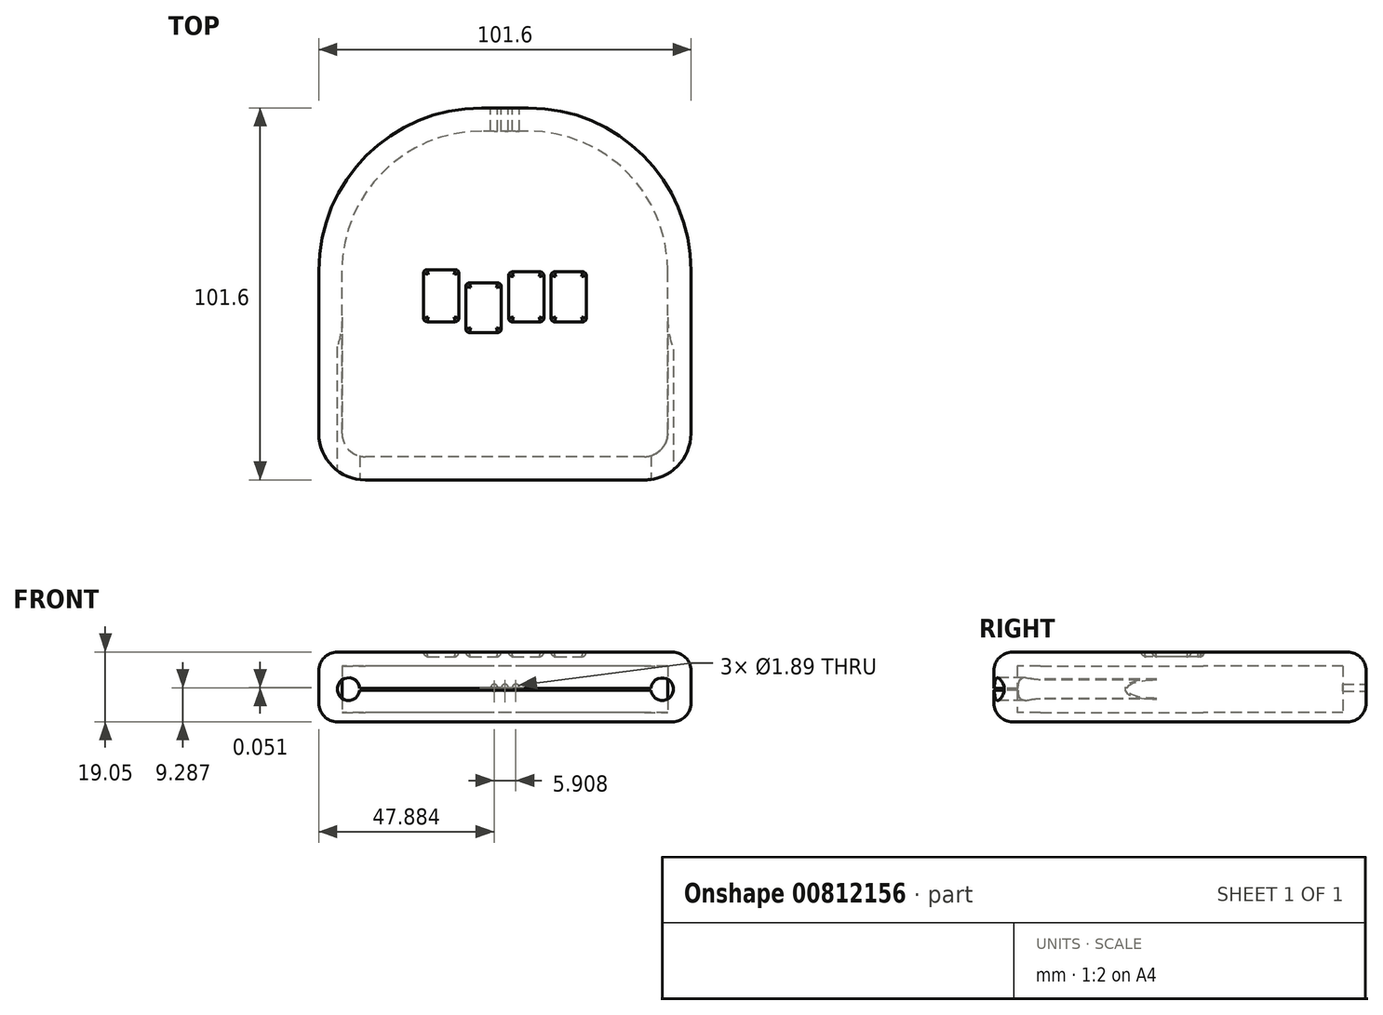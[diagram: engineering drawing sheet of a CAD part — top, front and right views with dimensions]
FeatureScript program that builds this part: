
annotation { "Feature Type Name" : "Feature", "Feature Type Description" : "" }
export const myFeature = defineFeature(function(context is Context, id is Id, definition is map)
    precondition{}
    {
        {
            var Q0;
            Q0=qCreatedBy(makeId("Top.planeOp"),FACE);
            cPlane(context, id + "F0", {"entities" : qUnion([Q0]), "cplaneType" : CPlaneType.OFFSET, "offset" : 2.54 * mm, "width" : 152.4 * mm, "height" : 152.4 * mm});
        }
        {
            var Q0;
            Q0=qCreatedBy(id+"F0.planeOp",FACE);
            var sketch = newSketch(context, id + "F1", { "sketchPlane" : qUnion([Q0])});
            skLineSegment(sketch, "E0.bottom", {"start": v(38.1, -44.45) * mm, "end": v(-38.1, -44.45) * mm});
            skLineSegment(sketch, "E0.top", {"start": v(6.35, 44.45) * mm, "end": v(-6.35, 44.45) * mm});
            skLineSegment(sketch, "E0.left", {"start": v(44.45, -38.1) * mm, "end": v(44.45, 6.35) * mm});
            skLineSegment(sketch, "E0.right", {"start": v(-44.45, -38.1) * mm, "end": v(-44.45, 6.35) * mm});
            skPoint(sketch, "E0.middle", {"position": v(0, 0) * mm});
            skPoint(sketch, "E1.visualSharp", {"position": v(-44.45, 44.45) * mm});
            skArc(sketch, "E1.filletArc", {"start": v(-6.35, 44.45) * mm, "mid": v(-33.3, 33.3) * mm, "end": v(-44.45, 6.35) * mm});
            skPoint(sketch, "E2.visualSharp", {"position": v(44.45, 44.45) * mm});
            skArc(sketch, "E2.filletArc", {"start": v(44.45, 6.35) * mm, "mid": v(33.3, 33.3) * mm, "end": v(6.35, 44.45) * mm});
            skPoint(sketch, "E3.visualSharp", {"position": v(-44.45, -44.45) * mm});
            skArc(sketch, "E3.filletArc", {"start": v(-44.45, -38.1) * mm, "mid": v(-42.6, -42.6) * mm, "end": v(-38.1, -44.45) * mm});
            skPoint(sketch, "E4.visualSharp", {"position": v(44.45, -44.45) * mm});
            skArc(sketch, "E4.filletArc", {"start": v(38.1, -44.45) * mm, "mid": v(42.6, -42.6) * mm, "end": v(44.45, -38.1) * mm});
            skSolve(sketch);
        }
        {
            var Q0;
            Q0=qCreatedBy(makeId("Top.planeOp"),FACE);
            var sketch = newSketch(context, id + "F2", { "sketchPlane" : qUnion([Q0])});
            skLineSegment(sketch, "E5.0", {"start": v(6.35, 50.8) * mm, "end": v(-6.35, 50.8) * mm});
            skArc(sketch, "E5.1", {"start": v(50.8, 6.35) * mm, "mid": v(37.78, 37.78) * mm, "end": v(6.35, 50.8) * mm});
            skArc(sketch, "E5.2", {"start": v(-6.35, 50.8) * mm, "mid": v(-37.78, 37.78) * mm, "end": v(-50.8, 6.35) * mm});
            skLineSegment(sketch, "E5.3", {"start": v(50.8, -38.1) * mm, "end": v(50.8, 6.35) * mm});
            skLineSegment(sketch, "E5.4", {"start": v(-50.8, -38.1) * mm, "end": v(-50.8, 6.35) * mm});
            skArc(sketch, "E5.5", {"start": v(-50.8, -38.1) * mm, "mid": v(-47.08, -47.08) * mm, "end": v(-38.1, -50.8) * mm});
            skLineSegment(sketch, "E5.6", {"start": v(38.1, -50.8) * mm, "end": v(-38.1, -50.8) * mm});
            skArc(sketch, "E5.7", {"start": v(38.1, -50.8) * mm, "mid": v(47.08, -47.08) * mm, "end": v(50.8, -38.1) * mm});
            skSolve(sketch);
        }
        {
            var Q0;
            Q0=qSketchRegion(id+"F2",true);
            extrude(context, id + "F3", {"entities" : qUnion([Q0]), "depth" : 19.05 * mm, "offsetDistance" : 25.4 * mm});
        }
        {
            var Q0;
            Q0=makeQuery(id+"F3.opExtrude","CAP_FACE",FACE,{"disambiguationData":[OSD([sQuery(id+"F2.wireOp",EDGE,"E5.0"),sQuery(id+"F2.wireOp",EDGE,"E5.1"),sQuery(id+"F2.wireOp",EDGE,"E5.2"),sQuery(id+"F2.wireOp",EDGE,"E5.3"),sQuery(id+"F2.wireOp",EDGE,"E5.4"),sQuery(id+"F2.wireOp",EDGE,"E5.5"),sQuery(id+"F2.wireOp",EDGE,"E5.6"),sQuery(id+"F2.wireOp",EDGE,"E5.7")])],"isStart":false});
            var Q1;
            Q1 = qSketchRegion(id + "F1", true);
            extrude(context, id + "F4", {"entities" : qUnion([Q0, Q1]), "operationType" : NewBodyOperationType.REMOVE, "depth" : 12.7 * mm, "offsetDistance" : 25.4 * mm});
        }
        {
            var Q0;
            Q0=makeQuery(id+"F3.opExtrude","CAP_EDGE",EDGE,{"disambiguationData":[OSD([sQuery(id+"F2.wireOp",EDGE,"E5.5")])],"isStart":false});
            fillet(context, id + "F5", {"entities" : qUnion([Q0]), "radius" : 5.08 * mm, "tangentPropagation" : true, "allowEdgeOverflow" : false});
        }
        {
            var Q0;
            Q0=makeQuery(id+"F3.opExtrude","CAP_EDGE",EDGE,{"disambiguationData":[OSD([sQuery(id+"F2.wireOp",EDGE,"E5.3")])],"isStart":true});
            fillet(context, id + "F6", {"entities" : qUnion([Q0]), "radius" : 5.08 * mm, "tangentPropagation" : true, "allowEdgeOverflow" : false});
        }
        {
            var Q0;
            Q0=qCreatedBy(makeId("Top.planeOp"),FACE);
            cPlane(context, id + "F7", {"entities" : qUnion([Q0]), "cplaneType" : CPlaneType.OFFSET, "offset" : 19.05 * mm, "width" : 152.4 * mm, "height" : 152.4 * mm});
        }
        {
            var Q0;
            Q0=qCreatedBy(id+"F7.planeOp",FACE);
            var sketch = newSketch(context, id + "F8", { "sketchPlane" : qUnion([Q0])});
            skLineSegment(sketch, "E6.bottom", {"start": v(-21.17, 6.64) * mm, "end": v(-13.57, 6.64) * mm});
            skLineSegment(sketch, "E6.top", {"start": v(-21.17, -7.6) * mm, "end": v(-13.57, -7.6) * mm});
            skLineSegment(sketch, "E6.left", {"start": v(-22.19, 5.62) * mm, "end": v(-22.19, -6.58) * mm});
            skLineSegment(sketch, "E6.right", {"start": v(-12.56, 5.62) * mm, "end": v(-12.56, -6.58) * mm});
            skPoint(sketch, "E7.visualSharp", {"position": v(-12.56, 6.64) * mm});
            skArc(sketch, "E7.filletArc", {"start": v(-12.56, 5.62) * mm, "mid": v(-12.85, 6.34) * mm, "end": v(-13.57, 6.64) * mm});
            skPoint(sketch, "E8.visualSharp", {"position": v(-22.19, 6.64) * mm});
            skArc(sketch, "E8.filletArc", {"start": v(-21.17, 6.64) * mm, "mid": v(-21.9, 6.34) * mm, "end": v(-22.19, 5.62) * mm});
            skPoint(sketch, "E9.visualSharp", {"position": v(-22.19, -7.6) * mm});
            skArc(sketch, "E9.filletArc", {"start": v(-22.19, -6.58) * mm, "mid": v(-21.9, -7.3) * mm, "end": v(-21.17, -7.6) * mm});
            skPoint(sketch, "E10.visualSharp", {"position": v(-12.56, -7.6) * mm});
            skArc(sketch, "E10.filletArc", {"start": v(-13.57, -7.6) * mm, "mid": v(-12.85, -7.3) * mm, "end": v(-12.56, -6.58) * mm});
            skLineSegment(sketch, "E11.bottom", {"start": v(-9.62, 3.05) * mm, "end": v(-2.02, 3.05) * mm});
            skLineSegment(sketch, "E11.top", {"start": v(-9.62, -10.58) * mm, "end": v(-2.02, -10.58) * mm});
            skLineSegment(sketch, "E11.left", {"start": v(-10.63, 2.04) * mm, "end": v(-10.63, -9.57) * mm});
            skLineSegment(sketch, "E11.right", {"start": v(-1, 2.04) * mm, "end": v(-1, -9.57) * mm});
            skArc(sketch, "E12.filletArc", {"start": v(-1, 2.04) * mm, "mid": v(-1.3, 2.75) * mm, "end": v(-2.02, 3.05) * mm});
            skArc(sketch, "E13.filletArc", {"start": v(-9.62, 3.05) * mm, "mid": v(-10.34, 2.75) * mm, "end": v(-10.63, 2.04) * mm});
            skArc(sketch, "E14.filletArc", {"start": v(-10.63, -9.57) * mm, "mid": v(-10.34, -10.28) * mm, "end": v(-9.62, -10.58) * mm});
            skArc(sketch, "E15.filletArc", {"start": v(-2.02, -10.58) * mm, "mid": v(-1.3, -10.28) * mm, "end": v(-1, -9.57) * mm});
            skLineSegment(sketch, "E16.bottom", {"start": v(2.03, 6) * mm, "end": v(9.63, 6) * mm});
            skLineSegment(sketch, "E16.top", {"start": v(2.03, -7.63) * mm, "end": v(9.63, -7.63) * mm});
            skLineSegment(sketch, "E16.left", {"start": v(1.02, 4.99) * mm, "end": v(1.02, -6.61) * mm});
            skLineSegment(sketch, "E16.right", {"start": v(10.65, 4.99) * mm, "end": v(10.65, -6.61) * mm});
            skArc(sketch, "E17.filletArc", {"start": v(10.65, 4.99) * mm, "mid": v(10.35, 5.7) * mm, "end": v(9.63, 6) * mm});
            skArc(sketch, "E18.filletArc", {"start": v(2.03, 6) * mm, "mid": v(1.31, 5.7) * mm, "end": v(1.02, 4.99) * mm});
            skArc(sketch, "E19.filletArc", {"start": v(1.02, -6.61) * mm, "mid": v(1.31, -7.33) * mm, "end": v(2.03, -7.63) * mm});
            skArc(sketch, "E20.filletArc", {"start": v(9.63, -7.63) * mm, "mid": v(10.35, -7.33) * mm, "end": v(10.65, -6.61) * mm});
            skLineSegment(sketch, "E21.bottom", {"start": v(13.61, 6.02) * mm, "end": v(21.21, 6.02) * mm});
            skLineSegment(sketch, "E21.top", {"start": v(13.61, -7.62) * mm, "end": v(21.21, -7.62) * mm});
            skLineSegment(sketch, "E21.left", {"start": v(12.6, 5) * mm, "end": v(12.6, -6.6) * mm});
            skLineSegment(sketch, "E21.right", {"start": v(22.23, 5) * mm, "end": v(22.23, -6.6) * mm});
            skArc(sketch, "E22.filletArc", {"start": v(22.23, 5) * mm, "mid": v(21.93, 5.72) * mm, "end": v(21.21, 6.02) * mm});
            skArc(sketch, "E23.filletArc", {"start": v(13.61, 6.02) * mm, "mid": v(12.9, 5.72) * mm, "end": v(12.6, 5) * mm});
            skArc(sketch, "E24.filletArc", {"start": v(12.6, -6.6) * mm, "mid": v(12.9, -7.32) * mm, "end": v(13.61, -7.62) * mm});
            skArc(sketch, "E25.filletArc", {"start": v(21.21, -7.62) * mm, "mid": v(21.93, -7.32) * mm, "end": v(22.23, -6.6) * mm});
            skSolve(sketch);
        }
        {
            var Q0;
            Q0=makeQuery(id+"F8.imprint","IMPRINT",FACE,{"disambiguationData":[TD([[makeQuery(id+"F8.imprint","IMPRINT",EDGE,{"derivedFrom":sQuery(id+"F8.wireOp",EDGE,"E6.bottom")}),-1.0]])]});
            var Q1;
            Q1=makeQuery(id+"F8.imprint","IMPRINT",FACE,{"disambiguationData":[TD([[makeQuery(id+"F8.imprint","IMPRINT",EDGE,{"derivedFrom":sQuery(id+"F8.wireOp",EDGE,"E11.bottom")}),-1.0]])]});
            var Q2;
            Q2=makeQuery(id+"F8.imprint","IMPRINT",FACE,{"disambiguationData":[TD([[makeQuery(id+"F8.imprint","IMPRINT",EDGE,{"derivedFrom":sQuery(id+"F8.wireOp",EDGE,"E16.bottom")}),-1.0]])]});
            var Q3;
            Q3=makeQuery(id+"F8.imprint","IMPRINT",FACE,{"disambiguationData":[TD([[makeQuery(id+"F8.imprint","IMPRINT",EDGE,{"derivedFrom":sQuery(id+"F8.wireOp",EDGE,"E21.bottom")}),-1.0]])]});
            extrude(context, id + "F9", {"entities" : qUnion([Q0, Q1, Q2, Q3]), "operationType" : NewBodyOperationType.REMOVE, "oppositeDirection" : true, "depth" : 1.27 * mm, "offsetDistance" : 25.4 * mm});
        }
        {
            var Q0;
            Q0=makeQuery(id+"F9.boolean.opBoolean","COPY",EDGE,{"derivedFrom":makeQuery(id+"F9.opExtrude","CAP_EDGE",EDGE,{"disambiguationData":[OSD([sQuery(id+"F8.wireOp",EDGE,"E6.bottom")])],"isStart":false})});
            var Q1;
            Q1=makeQuery(id+"F9.boolean.opBoolean","COPY",EDGE,{"derivedFrom":makeQuery(id+"F9.opExtrude","CAP_EDGE",EDGE,{"disambiguationData":[OSD([sQuery(id+"F8.wireOp",EDGE,"E11.bottom")])],"isStart":false})});
            var Q2;
            Q2=makeQuery(id+"F9.boolean.opBoolean","COPY",EDGE,{"derivedFrom":makeQuery(id+"F9.opExtrude","CAP_EDGE",EDGE,{"disambiguationData":[OSD([sQuery(id+"F8.wireOp",EDGE,"E16.bottom")])],"isStart":false})});
            var Q3;
            Q3=makeQuery(id+"F9.boolean.opBoolean","COPY",EDGE,{"derivedFrom":makeQuery(id+"F9.opExtrude","CAP_EDGE",EDGE,{"disambiguationData":[OSD([sQuery(id+"F8.wireOp",EDGE,"E21.bottom")])],"isStart":false})});
            fillet(context, id + "F10", {"entities" : qUnion([Q0, Q1, Q2, Q3]), "radius" : 1.27 * mm, "tangentPropagation" : true, "allowEdgeOverflow" : false});
        }
        {
            var Q0;
            Q0=makeQuery(id+"F3.opExtrude","SWEPT_FACE",FACE,{"disambiguationData":[OSD([sQuery(id+"F2.wireOp",EDGE,"E5.6")])]});
            var sketch = newSketch(context, id + "F11", { "sketchPlane" : qUnion([Q0])});
            skLineSegment(sketch, "E26.bottom", {"start": v(44.26, 9.18) * mm, "end": v(-44.26, 9.18) * mm});
            skLineSegment(sketch, "E26.top", {"start": v(44.26, 8.66) * mm, "end": v(-44.26, 8.66) * mm});
            skLineSegment(sketch, "E26.left", {"start": v(44.26, 9.18) * mm, "end": v(44.26, 8.66) * mm});
            skLineSegment(sketch, "E26.right", {"start": v(-44.26, 9.18) * mm, "end": v(-44.26, 8.66) * mm});
            skPoint(sketch, "E26.middle", {"position": v(0, 8.92) * mm});
            skCircle(sketch, "E27", {"center": v(42.94, 8.92) * mm, "radius": 3.08 * mm});
            skCircle(sketch, "E28", {"center": v(-42.68, 8.92) * mm, "radius": 3.09 * mm});
            skSolve(sketch);
        }
        {
            var Q0;
            {var subQ0=sQuery(id+"F11.wireOp",EDGE,"E26.left");Q0=makeQuery(id+"F11.imprint","IMPRINT",FACE,{"disambiguationData":[TD([[makeQuery(id+"F11.imprint","IMPRINT",EDGE,{"derivedFrom":subQ0}),1.0]])]});}
            var Q1;
            {var subQ0=sQuery(id+"F11.wireOp",EDGE,"E26.bottom");var subQ1=sQuery(id+"F2.wireOp",EDGE,"E5.6");var subQ2=makeQuery(id+"F3.opExtrude","SWEPT_EDGE",EDGE,{"disambiguationData":[OSD([subQ1,sQuery(id+"F2.wireOp",EDGE,"E5.7")])]});var subQ3=makeQuery(id+"F11.imprint","INTERSECT",VERTEX,{"derivedFrom":[subQ2,subQ0]});Q1=makeQuery(id+"F11.imprint","IMPRINT",FACE,{"disambiguationData":[TD([[makeQuery(id+"F11.imprint","IMPRINT",EDGE,{"disambiguationData":[TD([[subQ3,-1.0]])],"derivedFrom":subQ0}),1.0]])]});}
            var Q2;
            {var subQ0=sQuery(id+"F11.wireOp",EDGE,"E27");var subQ1=sQuery(id+"F11.wireOp",EDGE,"E26.bottom");var subQ2=makeQuery(id+"F11.imprint","INTERSECT",VERTEX,{"derivedFrom":[subQ1,subQ0]});Q2=makeQuery(id+"F11.imprint","IMPRINT",FACE,{"disambiguationData":[TD([[makeQuery(id+"F11.imprint","IMPRINT",EDGE,{"disambiguationData":[TD([[subQ2,-1.0]])],"derivedFrom":subQ0}),-1.0]])]});}
            var Q3;
            {var subQ0=sQuery(id+"F11.wireOp",EDGE,"E26.left");Q3=makeQuery(id+"F11.imprint","IMPRINT",FACE,{"disambiguationData":[TD([[makeQuery(id+"F11.imprint","IMPRINT",EDGE,{"derivedFrom":subQ0}),-1.0]])]});}
            var Q4;
            {var subQ0=sQuery(id+"F11.wireOp",EDGE,"E28");var subQ1=sQuery(id+"F11.wireOp",EDGE,"E26.bottom");var subQ2=makeQuery(id+"F11.imprint","INTERSECT",VERTEX,{"derivedFrom":[subQ1,subQ0]});Q4=makeQuery(id+"F11.imprint","IMPRINT",FACE,{"disambiguationData":[TD([[makeQuery(id+"F11.imprint","IMPRINT",EDGE,{"disambiguationData":[TD([[subQ2,1.0]])],"derivedFrom":subQ0}),-1.0]])]});}
            var Q5;
            {var subQ0=sQuery(id+"F11.wireOp",EDGE,"E26.right");Q5=makeQuery(id+"F11.imprint","IMPRINT",FACE,{"disambiguationData":[TD([[makeQuery(id+"F11.imprint","IMPRINT",EDGE,{"derivedFrom":subQ0}),1.0]])]});}
            var Q6;
            {var subQ0=sQuery(id+"F11.wireOp",EDGE,"E26.right");Q6=makeQuery(id+"F11.imprint","IMPRINT",FACE,{"disambiguationData":[TD([[makeQuery(id+"F11.imprint","IMPRINT",EDGE,{"derivedFrom":subQ0}),-1.0]])]});}
            var Q7;
            Q7=sQuery(id+"F11.wireOp",EDGE,"E27");
            var Q8;
            Q8=sQuery(id+"F11.wireOp",EDGE,"E26.top");
            var Q9;
            Q9=sQuery(id+"F11.wireOp",EDGE,"E26.bottom");
            var Q10;
            Q10=sQuery(id+"F11.wireOp",EDGE,"E28");
            extrude(context, id + "F12", {"entities" : qUnion([Q0, Q1, Q2, Q3, Q4, Q5, Q6]), "operationType" : NewBodyOperationType.REMOVE, "surfaceEntities" : qUnion([Q7, Q8, Q9, Q10]), "oppositeDirection" : true, "depth" : 19.05 * mm, "offsetDistance" : 25.4 * mm});
        }
        {
            var Q0;
            Q0=makeQuery(id+"F12.boolean.opBoolean","INTERSECT",EDGE,{"derivedFrom":[makeQuery(id+"F4.boolean.opBoolean","COPY",FACE,{"derivedFrom":makeQuery(id+"F4.opExtrude","SWEPT_FACE",FACE,{"disambiguationData":[OSD([sQuery(id+"F1.wireOp",EDGE,"E0.left")])]})}),makeQuery(id+"F12.opExtrude","CAP_FACE",FACE,{"disambiguationData":[OSD([sQuery(id+"F11.wireOp",EDGE,"E26.bottom"),sQuery(id+"F11.wireOp",EDGE,"E26.top"),sQuery(id+"F11.wireOp",EDGE,"E27"),sQuery(id+"F11.wireOp",EDGE,"E28")])],"isStart":false})]});
            var Q1;
            Q1=makeQuery(id+"F12.boolean.opBoolean","INTERSECT",EDGE,{"derivedFrom":[makeQuery(id+"F4.boolean.opBoolean","COPY",FACE,{"derivedFrom":makeQuery(id+"F4.opExtrude","SWEPT_FACE",FACE,{"disambiguationData":[OSD([sQuery(id+"F1.wireOp",EDGE,"E0.right")])]})}),makeQuery(id+"F12.opExtrude","CAP_FACE",FACE,{"disambiguationData":[OSD([sQuery(id+"F11.wireOp",EDGE,"E26.bottom"),sQuery(id+"F11.wireOp",EDGE,"E26.top"),sQuery(id+"F11.wireOp",EDGE,"E27"),sQuery(id+"F11.wireOp",EDGE,"E28")])],"isStart":false})]});
            fillet(context, id + "F13", {"entities" : qUnion([Q0, Q1]), "radius" : 25.4 * mm, "tangentPropagation" : true, "allowEdgeOverflow" : false});
        }
        {
            var Q0;
            Q0=makeQuery(id+"F3.opExtrude","SWEPT_FACE",FACE,{"disambiguationData":[OSD([sQuery(id+"F2.wireOp",EDGE,"E5.0")])]});
            var sketch = newSketch(context, id + "F14", { "sketchPlane" : qUnion([Q0])});
            skCircle(sketch, "E29", {"center": v(0, 9.3) * mm, "radius": 0.95 * mm});
            skCircle(sketch, "E30", {"center": v(2.92, 9.29) * mm, "radius": 0.95 * mm});
            skCircle(sketch, "E31", {"center": v(-3, 9.34) * mm, "radius": 0.95 * mm});
            skSolve(sketch);
        }
        {
            var Q0;
            Q0=makeQuery(id+"F14.imprint","IMPRINT",FACE,{"disambiguationData":[TD([[makeQuery(id+"F14.imprint","IMPRINT",EDGE,{"derivedFrom":sQuery(id+"F14.wireOp",EDGE,"E30")}),1.0]])]});
            var Q1;
            Q1=makeQuery(id+"F14.imprint","IMPRINT",FACE,{"disambiguationData":[TD([[makeQuery(id+"F14.imprint","IMPRINT",EDGE,{"derivedFrom":sQuery(id+"F14.wireOp",EDGE,"E29")}),1.0]])]});
            var Q2;
            Q2=makeQuery(id+"F14.imprint","IMPRINT",FACE,{"disambiguationData":[TD([[makeQuery(id+"F14.imprint","IMPRINT",EDGE,{"derivedFrom":sQuery(id+"F14.wireOp",EDGE,"E31")}),1.0]])]});
            var Q3;
            Q3=sQuery(id+"F14.wireOp",EDGE,"E30");
            var Q4;
            Q4=sQuery(id+"F14.wireOp",EDGE,"E31");
            var Q5;
            Q5=sQuery(id+"F14.wireOp",EDGE,"E29");
            extrude(context, id + "F15", {"entities" : qUnion([Q0, Q1, Q2]), "operationType" : NewBodyOperationType.REMOVE, "surfaceEntities" : qUnion([Q3, Q4, Q5]), "oppositeDirection" : true, "depth" : 7.62 * mm, "offsetDistance" : 25.4 * mm});
        }
    });
